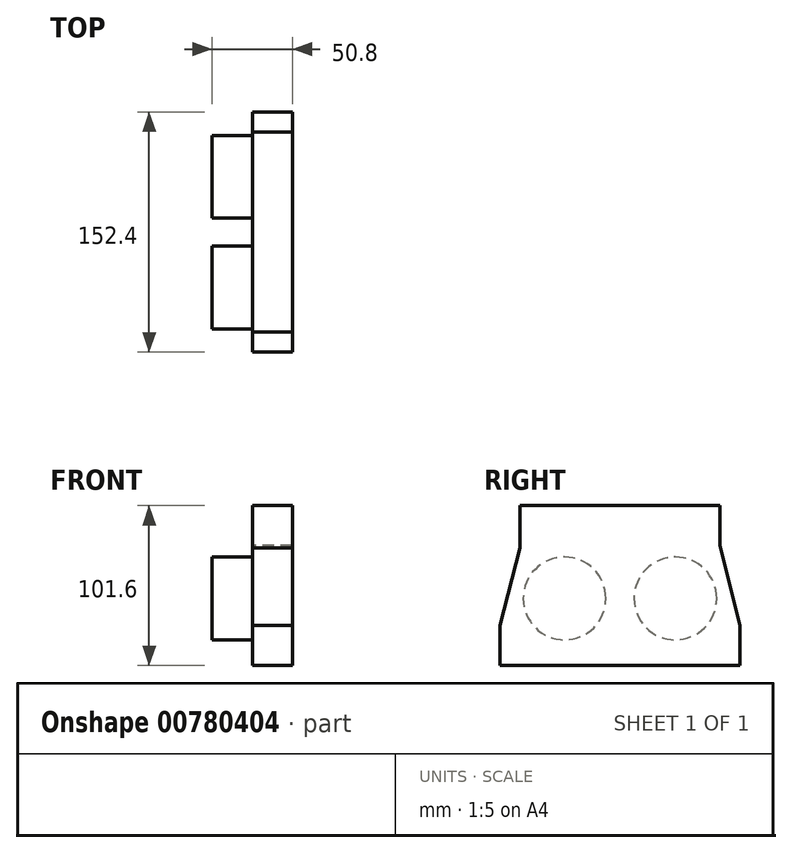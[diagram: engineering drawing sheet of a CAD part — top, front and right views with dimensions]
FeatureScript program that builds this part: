
annotation { "Feature Type Name" : "Feature", "Feature Type Description" : "" }
export const myFeature = defineFeature(function(context is Context, id is Id, definition is map)
    precondition{}
    {
        {
            var Q0;
            Q0=qCreatedBy(makeId("Right.planeOp"),FACE);
            var sketch = newSketch(context, id + "F0", { "sketchPlane" : qUnion([Q0])});
            skLineSegment(sketch, "E0.bottom", {"start": v(76.2, -42.57) * mm, "end": v(-76.2, -42.57) * mm});
            skLineSegment(sketch, "E0.top", {"start": v(76.2, -17.17) * mm, "end": v(-76.2, -17.17) * mm});
            skLineSegment(sketch, "E0.left", {"start": v(76.2, -42.57) * mm, "end": v(76.2, -17.17) * mm});
            skLineSegment(sketch, "E0.right", {"start": v(-76.2, -42.57) * mm, "end": v(-76.2, -17.17) * mm});
            skPoint(sketch, "E0.middle", {"position": v(0, -29.87) * mm});
            skLineSegment(sketch, "E1.bottom", {"start": v(-63.5, -17.17) * mm, "end": v(63.5, -17.17) * mm});
            skLineSegment(sketch, "E1.top", {"start": v(-63.5, 59.03) * mm, "end": v(63.5, 59.03) * mm});
            skLineSegment(sketch, "E1.left", {"start": v(-63.5, 32.02) * mm, "end": v(-63.5, 59.03) * mm});
            skLineSegment(sketch, "E1.right", {"start": v(63.5, 33.63) * mm, "end": v(63.5, 59.03) * mm});
            skLineSegment(sketch, "E2", {"start": v(-76.2, -17.17) * mm, "end": v(-63.5, 32.02) * mm});
            skLineSegment(sketch, "E3", {"start": v(76.2, -17.17) * mm, "end": v(63.5, 33.63) * mm});
            skSolve(sketch);
        }
        {
            var Q0;
            Q0=qSketchRegion(id+"F0",true);
            extrude(context, id + "F1", {"entities" : qUnion([Q0]), "depth" : 25.4 * mm, "offsetDistance" : 25.4 * mm});
        }
        {
            var Q0;
            Q0=qCreatedBy(makeId("Right.planeOp"),FACE);
            var sketch = newSketch(context, id + "F2", { "sketchPlane" : qUnion([Q0])});
            skCircle(sketch, "E4", {"center": v(35.2, 0) * mm, "radius": 26.25 * mm});
            skCircle(sketch, "E5", {"center": v(-35.2, 0) * mm, "radius": 26.25 * mm});
            skSolve(sketch);
        }
        {
            var Q0;
            Q0=qSketchRegion(id+"F2",true);
            extrude(context, id + "F3", {"entities" : qUnion([Q0]), "operationType" : NewBodyOperationType.ADD, "oppositeDirection" : true, "depth" : 25.4 * mm, "offsetDistance" : 25.4 * mm});
        }
    });
